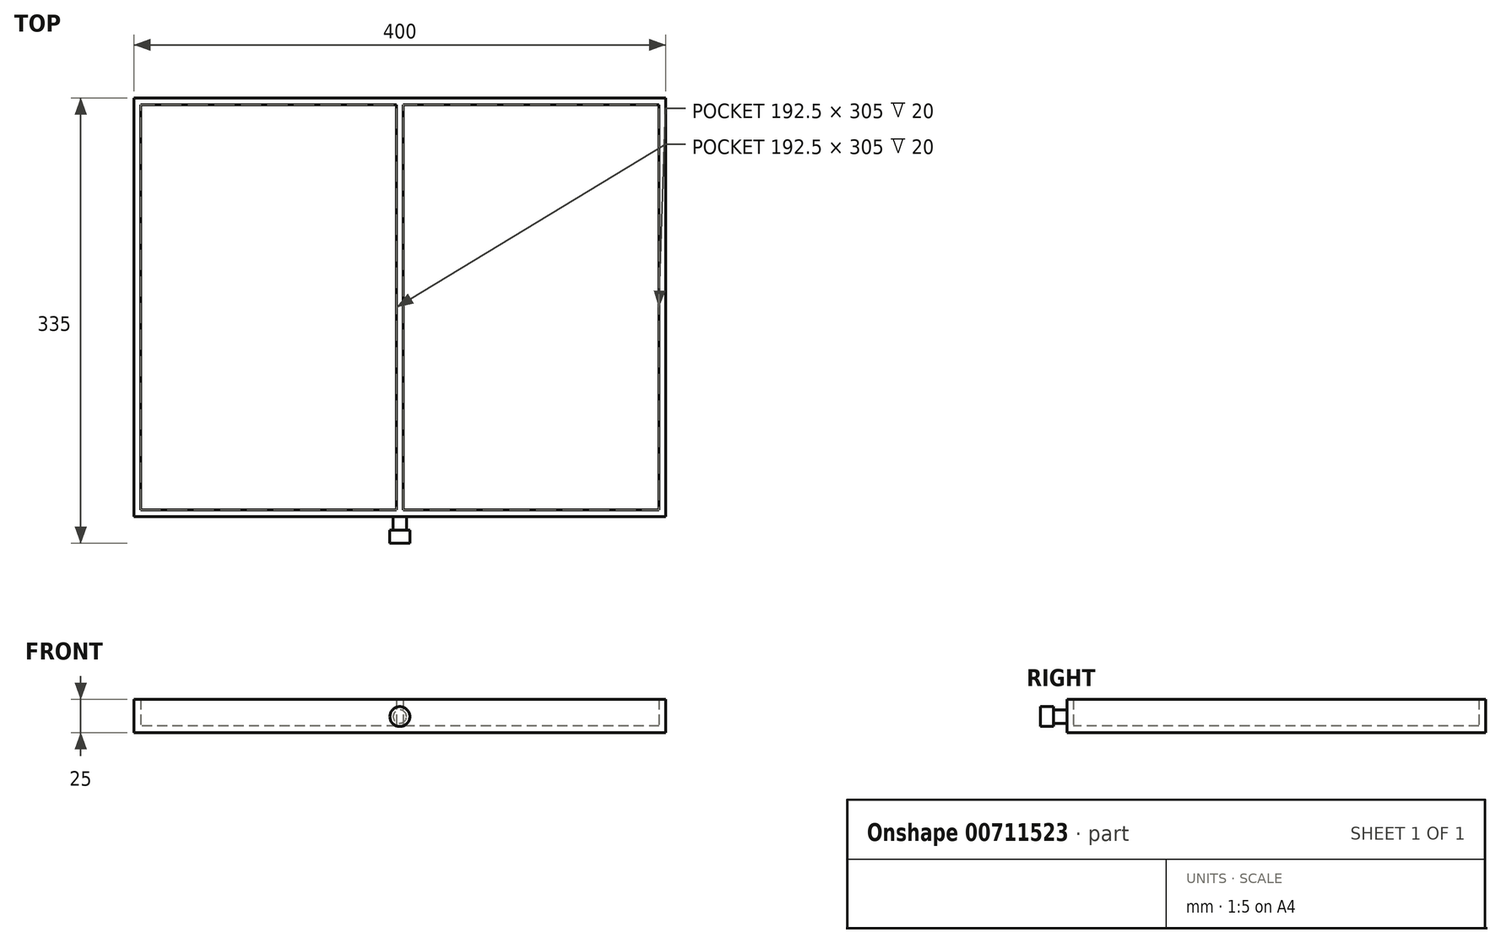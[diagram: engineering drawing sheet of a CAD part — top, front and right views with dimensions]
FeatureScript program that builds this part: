
annotation { "Feature Type Name" : "Feature", "Feature Type Description" : "" }
export const myFeature = defineFeature(function(context is Context, id is Id, definition is map)
    precondition{}
    {
        {
            var Q0;
            Q0=qCreatedBy(makeId("Top.planeOp"),FACE);
            var sketch = newSketch(context, id + "F0", { "sketchPlane" : qUnion([Q0])});
            skLineSegment(sketch, "E0.bottom", {"start": v(-33.22, 0) * mm, "end": v(5.14, 0) * mm});
            skLineSegment(sketch, "E0.top", {"start": v(-33.22, 42.2) * mm, "end": v(5.14, 42.2) * mm});
            skLineSegment(sketch, "E0.left", {"start": v(-33.22, 0) * mm, "end": v(-33.22, 42.2) * mm});
            skLineSegment(sketch, "E0.right", {"start": v(5.14, 0) * mm, "end": v(5.14, 42.2) * mm});
            skSolve(sketch);
        }
        {
            var Q0;
            Q0=makeQuery(id+"F0.imprint","IMPRINT",FACE,{"disambiguationData":[TD([[makeQuery(id+"F0.imprint","IMPRINT",EDGE,{"derivedFrom":sQuery(id+"F0.wireOp",EDGE,"E0.bottom")}),1.0]])]});
            extrude(context, id + "F1", {"entities" : qUnion([Q0]), "depth" : 0.69 * mm, "offsetDistance" : 25.4 * mm});
        }
        {
            var Q0;
            Q0=makeQuery(id+"F1.opExtrude","SWEPT_BODY",BODY,{"disambiguationData":[OSD([sQuery(id+"F0.wireOp",EDGE,"E0.bottom"),sQuery(id+"F0.wireOp",EDGE,"E0.top"),sQuery(id+"F0.wireOp",EDGE,"E0.left"),sQuery(id+"F0.wireOp",EDGE,"E0.right")])]});
            deleteBodies(context, id + "F2", {"entities" : qUnion([Q0])});
        }
        {
            var Q0;
            Q0=qCreatedBy(makeId("Top.planeOp"),FACE);
            var sketch = newSketch(context, id + "F3", { "sketchPlane" : qUnion([Q0])});
            skPoint(sketch, "E1.middle", {"position": v(0, 0) * mm});
            skLineSegment(sketch, "E2.bottom", {"start": v(200, -152.5) * mm, "end": v(-200, -152.5) * mm});
            skLineSegment(sketch, "E2.top", {"start": v(200, 152.5) * mm, "end": v(-200, 152.5) * mm});
            skLineSegment(sketch, "E2.left", {"start": v(200, -152.5) * mm, "end": v(200, 152.5) * mm});
            skLineSegment(sketch, "E2.right", {"start": v(-200, -152.5) * mm, "end": v(-200, 152.5) * mm});
            skSolve(sketch);
        }
        {
            var Q0;
            Q0 = qSketchRegion(id + "F3", true);
            extrude(context, id + "F4", {"entities" : qUnion([Q0]), "depth" : 5 * mm, "offsetDistance" : 25 * mm});
        }
        {
            var Q0;
            Q0=makeQuery(id+"F4.opExtrude","CAP_FACE",FACE,{"disambiguationData":[OSD([sQuery(id+"F3.wireOp",EDGE,"E2.bottom"),sQuery(id+"F3.wireOp",EDGE,"E2.top"),sQuery(id+"F3.wireOp",EDGE,"E2.left"),sQuery(id+"F3.wireOp",EDGE,"E2.right")])],"isStart":false});
            var sketch = newSketch(context, id + "F5", { "sketchPlane" : qUnion([Q0])});
            skLineSegment(sketch, "E3.bottom", {"start": v(-200, -152.5) * mm, "end": v(-195, -152.5) * mm});
            skLineSegment(sketch, "E3.top", {"start": v(-200, 152.5) * mm, "end": v(-195, 152.5) * mm});
            skLineSegment(sketch, "E3.left", {"start": v(-200, -152.5) * mm, "end": v(-200, 152.5) * mm});
            skLineSegment(sketch, "E3.right", {"start": v(-195, -152.5) * mm, "end": v(-195, 152.5) * mm});
            skSolve(sketch);
        }
        {
            var Q0;
            Q0 = qSketchRegion(id + "F5", true);
            extrude(context, id + "F6", {"entities" : qUnion([Q0]), "operationType" : NewBodyOperationType.ADD, "depth" : 20 * mm, "offsetDistance" : 25 * mm});
        }
        {
            var Q0;
            Q0=makeQuery(id+"F4.opExtrude","CAP_FACE",FACE,{"disambiguationData":[OSD([sQuery(id+"F3.wireOp",EDGE,"E2.bottom"),sQuery(id+"F3.wireOp",EDGE,"E2.top"),sQuery(id+"F3.wireOp",EDGE,"E2.left"),sQuery(id+"F3.wireOp",EDGE,"E2.right")])],"isStart":false});
            var sketch = newSketch(context, id + "F7", { "sketchPlane" : qUnion([Q0])});
            skLineSegment(sketch, "E4.bottom", {"start": v(200, 152.5) * mm, "end": v(195, 152.5) * mm});
            skLineSegment(sketch, "E4.top", {"start": v(200, -152.5) * mm, "end": v(195, -152.5) * mm});
            skLineSegment(sketch, "E4.left", {"start": v(200, 152.5) * mm, "end": v(200, -152.5) * mm});
            skLineSegment(sketch, "E4.right", {"start": v(195, 152.5) * mm, "end": v(195, -152.5) * mm});
            skSolve(sketch);
        }
        {
            var Q0;
            Q0 = qSketchRegion(id + "F7", true);
            extrude(context, id + "F8", {"entities" : qUnion([Q0]), "operationType" : NewBodyOperationType.ADD, "depth" : 20 * mm, "offsetDistance" : 25 * mm});
        }
        {
            var Q0;
            Q0=makeQuery(id+"F8.boolean.opBoolean","MERGE",FACE,{"derivedFrom":[makeQuery(id+"F6.boolean.opBoolean","MERGE",FACE,{"derivedFrom":[makeQuery(id+"F4.opExtrude","SWEPT_FACE",FACE,{"disambiguationData":[OSD([sQuery(id+"F3.wireOp",EDGE,"E2.top")])]}),makeQuery(id+"F6.opExtrude","SWEPT_FACE",FACE,{"disambiguationData":[OSD([sQuery(id+"F5.wireOp",EDGE,"E3.top")])]})]}),makeQuery(id+"F8.opExtrude","SWEPT_FACE",FACE,{"disambiguationData":[OSD([sQuery(id+"F7.wireOp",EDGE,"E4.bottom")])]})]});
            var sketch = newSketch(context, id + "F9", { "sketchPlane" : qUnion([Q0])});
            skLineSegment(sketch, "E5.bottom", {"start": v(-200, 0) * mm, "end": v(200, 0) * mm});
            skLineSegment(sketch, "E5.top", {"start": v(-200, 25) * mm, "end": v(200, 25) * mm});
            skLineSegment(sketch, "E5.left", {"start": v(-200, 0) * mm, "end": v(-200, 25) * mm});
            skLineSegment(sketch, "E5.right", {"start": v(200, 0) * mm, "end": v(200, 25) * mm});
            skSolve(sketch);
        }
        {
            var Q0;
            Q0 = qSketchRegion(id + "F9", true);
            extrude(context, id + "F10", {"entities" : qUnion([Q0]), "operationType" : NewBodyOperationType.ADD, "depth" : 5 * mm, "offsetDistance" : 25 * mm});
        }
        {
            var Q0;
            Q0=makeQuery(id+"F4.opExtrude","CAP_FACE",FACE,{"disambiguationData":[OSD([sQuery(id+"F3.wireOp",EDGE,"E2.bottom"),sQuery(id+"F3.wireOp",EDGE,"E2.top"),sQuery(id+"F3.wireOp",EDGE,"E2.left"),sQuery(id+"F3.wireOp",EDGE,"E2.right")])],"isStart":false});
            var sketch = newSketch(context, id + "F11", { "sketchPlane" : qUnion([Q0])});
            skLineSegment(sketch, "E6.bottom", {"start": v(-2.5, 152.5) * mm, "end": v(2.5, 152.5) * mm});
            skLineSegment(sketch, "E6.top", {"start": v(-2.5, -152.5) * mm, "end": v(2.5, -152.5) * mm});
            skLineSegment(sketch, "E6.left", {"start": v(-2.5, 152.5) * mm, "end": v(-2.5, -152.5) * mm});
            skLineSegment(sketch, "E6.right", {"start": v(2.5, 152.5) * mm, "end": v(2.5, -152.5) * mm});
            skPoint(sketch, "E7", {"position": v(0, 0) * mm});
            skLineSegment(sketch, "E8", {"start": v(0, 152.5) * mm, "end": v(0, -152.5) * mm, "construction": true});
            skSolve(sketch);
        }
        {
            var Q0;
            Q0=makeQuery(id+"F11.imprint","IMPRINT",FACE,{"disambiguationData":[TD([[makeQuery(id+"F11.imprint","IMPRINT",EDGE,{"derivedFrom":sQuery(id+"F11.wireOp",EDGE,"E6.bottom")}),1.0]])]});
            extrude(context, id + "F12", {"entities" : qUnion([Q0]), "operationType" : NewBodyOperationType.ADD, "depth" : 20 * mm, "offsetDistance" : 25 * mm});
        }
        {
            var Q0;
            Q0=makeQuery(id+"F12.boolean.opBoolean","MERGE",FACE,{"derivedFrom":[makeQuery(id+"F8.boolean.opBoolean","MERGE",FACE,{"derivedFrom":[makeQuery(id+"F6.boolean.opBoolean","MERGE",FACE,{"derivedFrom":[makeQuery(id+"F4.opExtrude","SWEPT_FACE",FACE,{"disambiguationData":[OSD([sQuery(id+"F3.wireOp",EDGE,"E2.bottom")])]}),makeQuery(id+"F6.opExtrude","SWEPT_FACE",FACE,{"disambiguationData":[OSD([sQuery(id+"F5.wireOp",EDGE,"E3.bottom")])]})]}),makeQuery(id+"F8.opExtrude","SWEPT_FACE",FACE,{"disambiguationData":[OSD([sQuery(id+"F7.wireOp",EDGE,"E4.top")])]})]}),makeQuery(id+"F12.opExtrude","SWEPT_FACE",FACE,{"disambiguationData":[OSD([sQuery(id+"F11.wireOp",EDGE,"E6.top")])]})]});
            var sketch = newSketch(context, id + "F13", { "sketchPlane" : qUnion([Q0])});
            skLineSegment(sketch, "E9.bottom", {"start": v(200, 0) * mm, "end": v(-200, 0) * mm});
            skLineSegment(sketch, "E9.top", {"start": v(200, 25) * mm, "end": v(-200, 25) * mm});
            skLineSegment(sketch, "E9.left", {"start": v(200, 0) * mm, "end": v(200, 25) * mm});
            skLineSegment(sketch, "E9.right", {"start": v(-200, 0) * mm, "end": v(-200, 25) * mm});
            skSolve(sketch);
        }
        {
            var Q0;
            Q0 = qSketchRegion(id + "F13", true);
            extrude(context, id + "F14", {"entities" : qUnion([Q0]), "operationType" : NewBodyOperationType.ADD, "depth" : 5 * mm, "offsetDistance" : 25 * mm});
        }
        {
            var Q0;
            Q0=makeQuery(id+"F14.opExtrude","CAP_FACE",FACE,{"disambiguationData":[OSD([sQuery(id+"F13.wireOp",EDGE,"E9.bottom"),sQuery(id+"F13.wireOp",EDGE,"E9.top"),sQuery(id+"F13.wireOp",EDGE,"E9.left"),sQuery(id+"F13.wireOp",EDGE,"E9.right")])],"isStart":false});
            var sketch = newSketch(context, id + "F15", { "sketchPlane" : qUnion([Q0])});
            skCircle(sketch, "E10", {"center": v(0, 12.1) * mm, "radius": 5 * mm});
            skLineSegment(sketch, "E11", {"start": v(0, 25) * mm, "end": v(0, 0) * mm, "construction": true});
            skSolve(sketch);
        }
        {
            var Q0;
            Q0=makeQuery(id+"F15.imprint","IMPRINT",FACE,{"disambiguationData":[TD([[makeQuery(id+"F15.imprint","IMPRINT",EDGE,{"derivedFrom":sQuery(id+"F15.wireOp",EDGE,"E10")}),1.0]])]});
            extrude(context, id + "F16", {"entities" : qUnion([Q0]), "operationType" : NewBodyOperationType.ADD, "depth" : 10 * mm, "offsetDistance" : 25 * mm});
        }
        {
            var Q0;
            Q0=makeQuery(id+"F16.opExtrude","CAP_FACE",FACE,{"disambiguationData":[OSD([sQuery(id+"F15.wireOp",EDGE,"E10")])],"isStart":false});
            var sketch = newSketch(context, id + "F17", { "sketchPlane" : qUnion([Q0])});
            skCircle(sketch, "E12", {"center": v(0, 12.1) * mm, "radius": 7.5 * mm});
            skSolve(sketch);
        }
        {
            var Q0;
            Q0=makeQuery(id+"F17.imprint","IMPRINT",FACE,{"disambiguationData":[TD([[makeQuery(id+"F17.imprint","IMPRINT",EDGE,{"derivedFrom":sQuery(id+"F17.wireOp",EDGE,"E12")}),1.0]])]});
            var Q1;
            Q1=makeQuery(id+"F17.imprint","IMPRINT",FACE,{"disambiguationData":[TD([[makeQuery(id+"F17.imprint","IMPRINT",EDGE,{"derivedFrom":makeQuery(id+"F16.opExtrude","CAP_EDGE",EDGE,{"disambiguationData":[OSD([sQuery(id+"F15.wireOp",EDGE,"E10")])],"isStart":false})}),1.0]])]});
            extrude(context, id + "F18", {"entities" : qUnion([Q0, Q1]), "operationType" : NewBodyOperationType.ADD, "depth" : 10 * mm, "offsetDistance" : 25 * mm});
        }
    });
